# Revit family: Diffuser-Carnes-SFTB-Fixed-T_Bar
name_source: partatom
category: Duct Accessories
revit_build: Autodesk Revit Architecture 2012 (Build: 20110309_2315(x64)
units: mm (PartAtom-declared; Revit-internal decimal feet)

## types (7) — shared parameters
Catalog = http://www.carnes.com
Default Elevation = 0"
Description = Square Stamped Louvered Diffusers
Diameter = 6"
Donn Fineline = http://www.carnes.com
Flow = 0 CFM
Inner Diameter B = 5 7/8"
Manufacturer = CARNES COMPANY
Model = SFTB
Product Page URL = http://www.carnes.com
Radius = 3"
Specification Sheet = http://www.carnes.com
Subcatagory = Air Distribution
Supply Connection = Diffuser Supply Connector
Supply Connector = Yes
URL = http://www.carnes.com
Unit = Metal - Carnes - Steel Galvanized
Width A = 23 3/4"

## type names (no varying parameters)
- SFTB 24x6
- SFTB 24x7
- SFTB 24x8
- SFTB 24x10
- SFTB 24x12
- SFTB 24x14
- SFTB 24x16

## geometry (parser evidence)
native form markers: Blend x2, Sweep x2
no freeform markers — native parametric forms only
